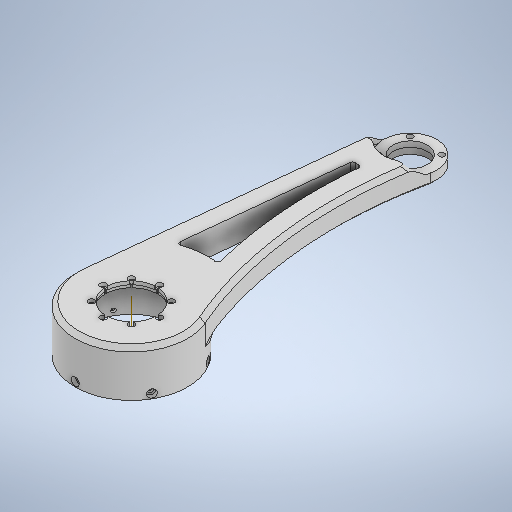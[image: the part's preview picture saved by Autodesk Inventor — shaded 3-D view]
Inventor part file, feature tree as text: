
AUTODESK INVENTOR PART (.ipt)
format: ipt  version: 2025.2 (Build 292293000, 293)  size: 1,673,728 bytes
history: native  units: mm
features: sketch x25, extrude x21, projected_geometry x21, fillet x6, other x2, plane x2, chamfer x2, pattern_circular x1
ambient origin geometry x8: Origin, YZ Plane, XZ Plane, XY Plane, X Axis, Y Axis, Z Axis, Center Point
bodies: Solid1 (feature_tree)
feature tree (80):
  other  "leg_wheel"
  extrude  "Extrusion1"  Depth=80.5mm
  extrude  "Extrusion2"  Depth=100.0mm
  extrude  "Extrusion3"  Depth=19.05mm
  extrude  "Extrusion4"  Depth=26.065mm
  extrude  "Extrusion5"  Depth=0.85mm
  extrude  "Extrusion6"  Depth=4.0mm
  extrude  "Extrusion7"  Depth=300.0mm
  extrude  "Extrusion8"  Depth=6.0mm TaperAngle=0.0deg
  extrude  "Extrusion9"  Depth=24.1mm TaperAngle=0.0deg
  extrude  "Extrusion12"  Depth=1.0mm
  extrude  "Extrusion13"  Depth=2.4mm TaperAngle=0.0deg
  extrude  "Extrusion14"  Depth=2.4mm
  extrude  "Extrusion15"  TaperAngle=0.0deg  [1 undecoded]
  extrude  "Extrusion16"  Depth=0.2mm
  plane  "Work Plane2"
  extrude  "Extrusion17"  Depth=0.2mm
  extrude  "Extrusion18"  Depth=2.5mm TaperAngle=0.0deg
  pattern_circular  "Circular Pattern1"  Count=8 Angle=360.0deg
  extrude  "Extrusion19"  Depth=0.8mm TaperAngle=0.0deg
  extrude  "Extrusion20"  Depth=0.8mm TaperAngle=0.0deg
  fillet  "Fillet2"  [1 undecoded]
  chamfer  "Chamfer1"  Distance=3.0mm
  fillet  "Fillet3"  Radius=3.0mm
  chamfer  "Chamfer2"  Distance=7.233mm
  extrude  "Extrusion21"  Depth=20.3mm
  extrude  "Extrusion22"  Depth=4.0mm TaperAngle=0.0deg
  fillet  "Fillet5"  Radius=12.0mm
  fillet  "Fillet6"  Radius=11.15mm
  extrude  "Extrusion23"  Depth=1.7mm TaperAngle=0.0deg
  fillet  "Fillet7"  Radius=1.7mm
  fillet  "Fillet8"  Radius=3.0mm
  sketch  "Sketch1"  dims[d0=38.0mm d1=80.5mm]
  sketch  "Sketch2"  dims[d7=9.0mm d8=0.0mm d10=19.05mm]
  projected_geometry  "Projected Loop1"
  sketch  "Sketch3"  dims[d14=5.0mm d15=0.0mm d16=0.85mm]
  sketch  "Sketch4"  dims[d17=0.0mm d18=0.0mm d19=4.0mm]
  sketch  "Sketch5"  dims[d21=45.0deg d23=300.0mm]
  sketch  "Sketch Circular Pattern1"  dims[d2=200.0mm d3=100.0mm]
  projected_geometry  "Projected Loop2"
  sketch  "Sketch6"  dims[d24=40.0mm d26=360.0deg d28=6.0mm d29=0.0mm]
  sketch  "Sketch7"  dims[d33=34.0mm d34=1.0mm]
  sketch  "Sketch8"  dims[d40=40.5mm d41=2.4mm]
  sketch  "Sketch9"  dims[d42=80.0mm d44=360.0deg d46=0.0mm d47=0.0mm]
  sketch  "Sketch Circular Pattern2"  dims[d11=9.0mm d12=0.0mm d13=26.065mm]
  sketch  "Sketch12"  dims[d68=4.4mm d69=0.2mm]
  projected_geometry  "Projected Loop5"
  sketch  "Sketch Circular Pattern6"  dims[d30=70.5mm d31=24.1mm d32=0.0mm]
  sketch  "Sketch13"  dims[d70=2.2mm d71=0.2mm]
  projected_geometry  "Projected Loop6"
  sketch  "Sketch Circular Pattern7"  dims[d35=4.1mm d36=0.0mm d38=2.4mm d39=0.0mm]
  sketch  "Sketch14"  dims[d72=80.0mm d74=360.0deg d76=2.5mm d77=0.0mm]
  projected_geometry  "Projected Loop7"
  projected_geometry  "Projected Loop8"
  projected_geometry  "Projected Loop9"
  projected_geometry  "Projected Loop10"
  projected_geometry  "Projected Loop11"
  projected_geometry  "Projected Loop12"
  projected_geometry  "Projected Loop13"
  projected_geometry  "Projected Loop14"
  sketch  "Sketch15"  dims[d79=37.0mm]
  projected_geometry  "Projected Loop15"
  projected_geometry  "Projected Loop16"
  projected_geometry  "Projected Loop17"
  projected_geometry  "Projected Loop18"
  projected_geometry  "Projected Loop19"
  projected_geometry  "Projected Loop20"
  projected_geometry  "Projected Loop21"
  projected_geometry  "Projected Loop22"
  sketch  "Sketch16"  dims[d80=0.3mm]
  projected_geometry  "Projected Loop23"
  other  "Work Axis1"
  plane  "Work Plane1"
  sketch  "Sketch17"  dims[d81=0.2mm]
  sketch  "Sketch18"  dims[d82=0.2mm d83=80.0mm d85=360.0deg]
  sketch  "Sketch19"  dims[d87=0.0mm d88=0.0mm d89=0.8mm d90=0.0mm]
  sketch  "Sketch20"  dims[d91=0.1mm d92=0.0mm d93=0.8mm d94=0.0mm d95=-5.235988mm]
  sketch  "Sketch21"  dims[d96=3.35mm]
  sketch  "Sketch22"  dims[d97=5.7mm d98=3.0mm d99=0.0mm d100=3.0mm d101=7.233mm d102=0.0mm]
  sketch  "Sketch23"  dims[d103=50.0mm d104=240.0deg d106=20.3mm d107=4.0mm d108=0.0mm d109=12.0mm d110=11.15mm d111=1.7mm d112=0.0mm d113=1.7mm d114=3.0mm d115=2.0mm d116=45.0deg d117=3.0mm d118=3.0mm d119=2.0mm d120=45.0deg d121=1.2mm d122=1.2mm d123=5.0mm d124=5.0mm d125=27.1mm d126=0.0mm d127=24.0mm d128=0.0mm d130=2.9mm d131=2.9mm d132=15.0mm d134=15.0mm d135=15.0mm d136=0.0mm d137=0.0mm d138=2.0mm d139=3.0mm d140=0.0mm d141=0.0mm d142=0.0mm d143=0.0mm]
note: 2 required parameter values undecoded (feature->parameter linkage not recoverable at this tier; creation-order binding heuristic only, values carry confidence <= 0.55)
